# Revit family: FU_Table_Sandler_Corda 162-75
name_source: partatom
category: Furniture
units: mm (PartAtom-declared; Revit-internal decimal feet)

## family parameters
Always vertical = Yes
Cut with Voids When Loaded = No
OmniClass Number = 23.40.20.00
OmniClass Title = General Furniture and Specialties
Room Calculation Point = No
Shared = No
Work Plane-Based = No

## types (1)
- FU_Table_Sandler_Corda 162-75
    Default Elevation = 0 mm  [stored 0 ft]
    Depth = 800 mm  [stored 2.62467 ft]
    Description = Table with stratified laminate top on a powder coated steel base. Suitable for outdoor use. Diam. 32”
    Frame Finish = Metal Lacquers - Burnished Brown
    HPL Top = HPL - Solid - White
    Height = 1090 mm  [stored 3.57612 ft]
    Manufacturer = Sandler
    Model = Corda Table 162.75
    URL = https://www.sandlerseating.com
    Width = 800 mm  [stored 2.62467 ft]

note: [stored X ft] marks values corroborated as IEEE doubles in the binary element streams (Revit-internal decimal feet)

## geometry (parser evidence)
native form markers: Sweep x2
no freeform markers — native parametric forms only
